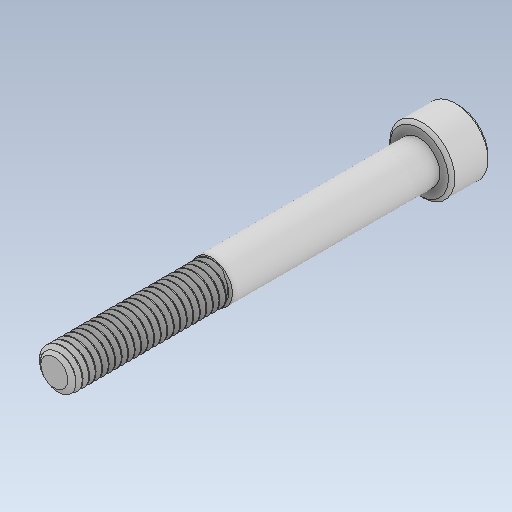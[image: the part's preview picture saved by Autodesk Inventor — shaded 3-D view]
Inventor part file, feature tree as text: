
AUTODESK INVENTOR PART (.ipt)
format: ipt  version: 2023 (Build 270158000, 158)  size: 626,688 bytes
history: native  units: in
note: dims shown in document units (in); Inventor stores cm internally (conversion verified against a paired STEP export)
features: chamfer x1
ambient origin geometry x8: Origin, YZ Plane, XZ Plane, XY Plane, X Axis, Y Axis, Z Axis, Center Point
bodies: Solid1 (feature_tree)
feature tree (1):
  chamfer  "Chamfer1"  [1 undecoded]
note: 1 required parameter value undecoded (feature->parameter linkage not recoverable at this tier; creation-order binding heuristic only, values carry confidence <= 0.55)
